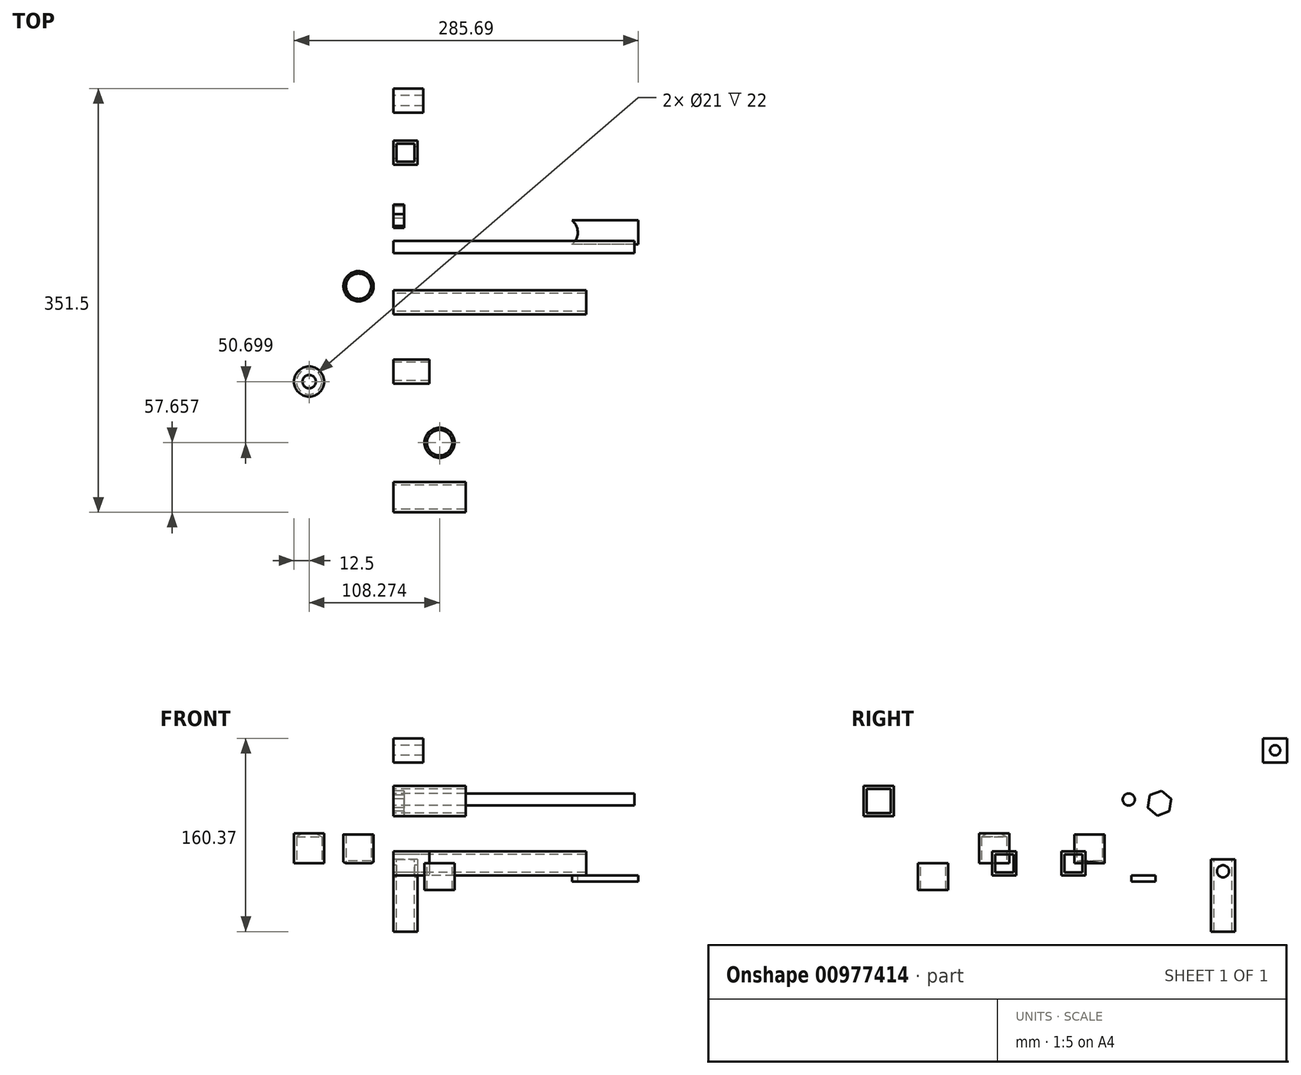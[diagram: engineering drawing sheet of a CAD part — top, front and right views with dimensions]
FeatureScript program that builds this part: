
annotation { "Feature Type Name" : "Feature", "Feature Type Description" : "" }
export const myFeature = defineFeature(function(context is Context, id is Id, definition is map)
    precondition{}
    {
        {
            var Q0;
            Q0=qCreatedBy(makeId("Front.planeOp"),FACE);
            var sketch = newSketch(context, id + "F0", { "sketchPlane" : qUnion([Q0])});
            skLineSegment(sketch, "E0.bottom", {"start": v(160, 10) * mm, "end": v(0, 10) * mm});
            skLineSegment(sketch, "E0.top", {"start": v(160, -10) * mm, "end": v(0, -10) * mm});
            skLineSegment(sketch, "E0.left", {"start": v(160, 10) * mm, "end": v(160, -10) * mm});
            skLineSegment(sketch, "E0.right", {"start": v(0, 10) * mm, "end": v(0, -10) * mm});
            skPoint(sketch, "E0.middle", {"position": v(80, 0) * mm});
            skSolve(sketch);
        }
        {
            var Q0;
            Q0 = qSketchRegion(id + "F0", true);
            extrude(context, id + "F1", {"entities" : qUnion([Q0]), "endBound" : BoundingType.SYMMETRIC, "depth" : 20 * mm, "offsetDistance" : 25 * mm});
        }
        {
            var Q0;
            Q0=qCreatedBy(makeId("Right.planeOp"),FACE);
            var sketch = newSketch(context, id + "F2", { "sketchPlane" : qUnion([Q0])});
            skLineSegment(sketch, "E1.bottom", {"start": v(-149.11, 64.26) * mm, "end": v(-174.11, 64.26) * mm});
            skLineSegment(sketch, "E1.top", {"start": v(-149.11, 39.26) * mm, "end": v(-174.11, 39.26) * mm});
            skLineSegment(sketch, "E1.left", {"start": v(-149.11, 64.26) * mm, "end": v(-149.11, 39.26) * mm});
            skLineSegment(sketch, "E1.right", {"start": v(-174.11, 64.26) * mm, "end": v(-174.11, 39.26) * mm});
            skPoint(sketch, "E1.middle", {"position": v(-161.61, 51.76) * mm});
            skLineSegment(sketch, "E2.bottom", {"start": v(-151.61, 61.76) * mm, "end": v(-171.61, 61.76) * mm});
            skLineSegment(sketch, "E2.top", {"start": v(-151.61, 41.76) * mm, "end": v(-171.61, 41.76) * mm});
            skLineSegment(sketch, "E2.left", {"start": v(-151.61, 61.76) * mm, "end": v(-151.61, 41.76) * mm});
            skLineSegment(sketch, "E2.right", {"start": v(-171.61, 61.76) * mm, "end": v(-171.61, 41.76) * mm});
            skSolve(sketch);
        }
        {
            var Q0;
            Q0 = qSketchRegion(id + "F2", true);
            extrude(context, id + "F3", {"entities" : qUnion([Q0]), "depth" : 60 * mm, "offsetDistance" : 25 * mm});
        }
        {
            var Q0;
            Q0=qCreatedBy(makeId("Right.planeOp"),FACE);
            var sketch = newSketch(context, id + "F4", { "sketchPlane" : qUnion([Q0])});
            skLineSegment(sketch, "E3.bottom", {"start": v(-7.5, 7.5) * mm, "end": v(7.5, 7.5) * mm});
            skLineSegment(sketch, "E3.top", {"start": v(-7.5, -7.5) * mm, "end": v(7.5, -7.5) * mm});
            skLineSegment(sketch, "E3.left", {"start": v(-7.5, 7.5) * mm, "end": v(-7.5, -7.5) * mm});
            skLineSegment(sketch, "E3.right", {"start": v(7.5, 7.5) * mm, "end": v(7.5, -7.5) * mm});
            skPoint(sketch, "E3.middle", {"position": v(0, 0) * mm});
            skSolve(sketch);
        }
        {
            var Q0;
            Q0 = qSketchRegion(id + "F4", true);
            extrude(context, id + "F5", {"entities" : qUnion([Q0]), "operationType" : NewBodyOperationType.REMOVE, "depth" : 160 * mm, "offsetDistance" : 25 * mm});
        }
        {
            var Q0;
            Q0=qCreatedBy(makeId("Right.planeOp"),FACE);
            var sketch = newSketch(context, id + "F6", { "sketchPlane" : qUnion([Q0])});
            skLineSegment(sketch, "E4.bottom", {"start": v(-67.3, 9.88) * mm, "end": v(-47.3, 9.88) * mm});
            skLineSegment(sketch, "E4.top", {"start": v(-67.3, -10.12) * mm, "end": v(-47.3, -10.12) * mm});
            skLineSegment(sketch, "E4.left", {"start": v(-67.3, 9.88) * mm, "end": v(-67.3, -10.12) * mm});
            skLineSegment(sketch, "E4.right", {"start": v(-47.3, 9.88) * mm, "end": v(-47.3, -10.12) * mm});
            skPoint(sketch, "E4.middle", {"position": v(-57.3, -0.12) * mm});
            skLineSegment(sketch, "E5.bottom", {"start": v(-64.8, 7.38) * mm, "end": v(-49.8, 7.38) * mm});
            skLineSegment(sketch, "E5.top", {"start": v(-64.8, -7.62) * mm, "end": v(-49.8, -7.62) * mm});
            skLineSegment(sketch, "E5.left", {"start": v(-64.8, 7.38) * mm, "end": v(-64.8, -7.62) * mm});
            skLineSegment(sketch, "E5.right", {"start": v(-49.8, 7.38) * mm, "end": v(-49.8, -7.62) * mm});
            skSolve(sketch);
        }
        {
            var Q0;
            Q0 = qSketchRegion(id + "F6", true);
            extrude(context, id + "F7", {"entities" : qUnion([Q0]), "depth" : 30 * mm, "offsetDistance" : 25 * mm});
        }
        {
            var Q0;
            Q0=qCreatedBy(makeId("Top.planeOp"),FACE);
            var sketch = newSketch(context, id + "F8", { "sketchPlane" : qUnion([Q0])});
            skCircle(sketch, "E6", {"center": v(38.4, -116.45) * mm, "radius": 12.5 * mm});
            skCircle(sketch, "E7", {"center": v(38.4, -116.45) * mm, "radius": 10.5 * mm});
            skSolve(sketch);
        }
        {
            var Q0;
            Q0 = qSketchRegion(id + "F8", true);
            extrude(context, id + "F9", {"entities" : qUnion([Q0]), "oppositeDirection" : true, "depth" : 22 * mm, "offsetDistance" : 25 * mm});
        }
        {
            var Q0;
            Q0=qCreatedBy(makeId("Top.planeOp"),FACE);
            var sketch = newSketch(context, id + "F10", { "sketchPlane" : qUnion([Q0])});
            skCircle(sketch, "E8", {"center": v(-28.9, 13.35) * mm, "radius": 12.5 * mm});
            skCircle(sketch, "E9", {"center": v(-28.9, 13.35) * mm, "radius": 10.5 * mm});
            skSolve(sketch);
        }
        {
            var Q0;
            Q0 = qSketchRegion(id + "F10", true);
            extrude(context, id + "F11", {"entities" : qUnion([Q0]), "operationType" : NewBodyOperationType.ADD, "depth" : 24 * mm, "offsetDistance" : 25 * mm});
        }
        {
            var Q0;
            Q0=qCreatedBy(makeId("Top.planeOp"),FACE);
            var sketch = newSketch(context, id + "F12", { "sketchPlane" : qUnion([Q0])});
            skCircle(sketch, "E10", {"center": v(-69.87, -65.75) * mm, "radius": 12.5 * mm});
            skSolve(sketch);
        }
        {
            var Q0;
            Q0=makeQuery(id+"F12.imprint","IMPRINT",FACE,{"disambiguationData":[TD([[makeQuery(id+"F12.imprint","IMPRINT",EDGE,{"derivedFrom":sQuery(id+"F12.wireOp",EDGE,"E10")}),1.0]])]});
            var Q1;
            Q1=sQuery(id+"F12.wireOp",EDGE,"E10");
            extrude(context, id + "F13", {"entities" : qUnion([Q0]), "surfaceEntities" : qUnion([Q1]), "depth" : 25 * mm, "offsetDistance" : 25 * mm});
        }
        {
            var Q0;
            Q0=sQuery(id+"F12.wireOp",VERTEX,"E10.center");
            var Q1;
            Q1=makeQuery(id+"F13.opExtrude","SWEPT_BODY",BODY,{"disambiguationData":[OSD([sQuery(id+"F12.wireOp",EDGE,"E10")])]});
            hole(context, id + "F14", {"style" : HoleStyle.SIMPLE, "endStyle" : HoleEndStyle.BLIND, "oppositeDirection" : true, "holeDiameter" : 21 * mm, "majorDiameter" : 5 * mm, "holeDepth" : 22 * mm, "isTappedThrough" : true, "tappedDepth" : 12 * mm, "tapClearance" : 3, "locations" : qUnion([Q0]), "scope" : qUnion([Q1])});
        }
        {
            var Q0;
            Q0=makeQuery(id+"F1.opExtrude","SWEPT_FACE",FACE,{"disambiguationData":[OSD([sQuery(id+"F0.wireOp",EDGE,"E0.top")])]});
            var sketch = newSketch(context, id + "F15", { "sketchPlane" : qUnion([Q0])});
            skLineSegment(sketch, "E11.bottom", {"start": v(203.32, -48.1) * mm, "end": v(148.32, -48.1) * mm});
            skLineSegment(sketch, "E11.top", {"start": v(203.32, -68.1) * mm, "end": v(148.32, -68.1) * mm});
            skLineSegment(sketch, "E11.left", {"start": v(203.32, -48.1) * mm, "end": v(203.32, -68.1) * mm});
            skLineSegment(sketch, "E11.right", {"start": v(148.32, -48.1) * mm, "end": v(148.32, -68.1) * mm});
            skPoint(sketch, "E11.middle", {"position": v(175.82, -58.1) * mm});
            skSolve(sketch);
        }
        {
            var Q0;
            Q0 = qSketchRegion(id + "FznQOVtNDYuo7BJ_6", true);
            var Q1;
            Q1=makeQuery(id+"F15.imprint","IMPRINT",FACE,{"disambiguationData":[TD([[makeQuery(id+"F15.imprint","IMPRINT",EDGE,{"derivedFrom":sQuery(id+"F15.wireOp",EDGE,"E11.bottom")}),1.0]])]});
            extrude(context, id + "F16", {"entities" : qUnion([Q0, Q1]), "depth" : 5 * mm, "offsetDistance" : 25 * mm});
        }
        {
            var Q0;
            Q0=qCreatedBy(makeId("Right.planeOp"),FACE);
            var sketch = newSketch(context, id + "F17", { "sketchPlane" : qUnion([Q0])});
            skLineSegment(sketch, "E12.bottom", {"start": v(134.15, 3.4) * mm, "end": v(114.15, 3.4) * mm});
            skLineSegment(sketch, "E12.top", {"start": v(134.15, -56.6) * mm, "end": v(114.15, -56.6) * mm});
            skLineSegment(sketch, "E12.left", {"start": v(134.15, 3.4) * mm, "end": v(134.15, -56.6) * mm});
            skLineSegment(sketch, "E12.right", {"start": v(114.15, 3.4) * mm, "end": v(114.15, -56.6) * mm});
            skPoint(sketch, "E12.middle", {"position": v(124.15, -26.6) * mm});
            skPoint(sketch, "E13", {"position": v(124.15, -6.6) * mm});
            skCircle(sketch, "E14", {"center": v(124.15, -6.6) * mm, "radius": 5 * mm});
            skSolve(sketch);
        }
        {
            var Q0;
            Q0 = qSketchRegion(id + "F17", true);
            extrude(context, id + "F18", {"entities" : qUnion([Q0]), "depth" : 20 * mm, "offsetDistance" : 25 * mm});
        }
        {
            var Q0;
            Q0=qCreatedBy(makeId("Right.planeOp"),FACE);
            var sketch = newSketch(context, id + "F19", { "sketchPlane" : qUnion([Q0])});
            skLineSegment(sketch, "E15.bottom", {"start": v(177.39, 103.76) * mm, "end": v(157.39, 103.76) * mm});
            skLineSegment(sketch, "E15.top", {"start": v(177.39, 83.76) * mm, "end": v(157.39, 83.76) * mm});
            skLineSegment(sketch, "E15.left", {"start": v(177.39, 103.76) * mm, "end": v(177.39, 83.76) * mm});
            skLineSegment(sketch, "E15.right", {"start": v(157.39, 103.76) * mm, "end": v(157.39, 83.76) * mm});
            skPoint(sketch, "E15.middle", {"position": v(167.39, 93.76) * mm});
            skSolve(sketch);
        }
        {
            var Q0;
            Q0=makeQuery(id+"F19.imprint","IMPRINT",FACE,{"disambiguationData":[TD([[makeQuery(id+"F19.imprint","IMPRINT",EDGE,{"derivedFrom":sQuery(id+"F19.wireOp",EDGE,"E15.bottom")}),1.0]])]});
            var Q1;
            Q1=makeQuery(id+"F19.imprint","IMPRINT",FACE,{"disambiguationData":[TD([[makeQuery(id+"F19.imprint","IMPRINT",EDGE,{"derivedFrom":sQuery(id+"F19.wireOp",EDGE,"7127c330-42ca-4884-bdbb-8791a35309d2")}),1.0]])]});
            extrude(context, id + "F20", {"entities" : qUnion([Q0, Q1]), "depth" : 25 * mm, "offsetDistance" : 25 * mm});
        }
        {
            var Q0;
            Q0=sQuery(id+"F19.wireOp",VERTEX,"E15.middle");
            var Q1;
            Q1=makeQuery(id+"F20.opExtrude","SWEPT_BODY",BODY,{"disambiguationData":[OSD([sQuery(id+"F19.wireOp",EDGE,"E15.bottom"),sQuery(id+"F19.wireOp",EDGE,"E15.top"),sQuery(id+"F19.wireOp",EDGE,"E15.left"),sQuery(id+"F19.wireOp",EDGE,"E15.right")])]});
            hole(context, id + "F21", {"style" : HoleStyle.SIMPLE, "endStyle" : HoleEndStyle.THROUGH, "oppositeDirection" : true, "standardTappedOrClearance" : lookupTablePath({ "fit" : "Normal", "standard" : "ISO", "engagement" : "75%", "pitch" : "1.5 mm", "size" : "M10", "type" : "Tapped" }), "standardBlindInLast" : lookupTablePath({ "fit" : "Normal", "standard" : "ISO", "engagement" : "75%", "pitch" : "1.5 mm", "size" : "M10", "type" : "Clearance & tapped" }), "holeDiameter" : 8.5 * mm, "majorDiameter" : 10 * mm, "showTappedDepth" : true, "isTappedThrough" : true, "tappedDepth" : 12 * mm, "tapClearance" : 3, "locations" : qUnion([Q0]), "scope" : qUnion([Q1])});
        }
        {
            var Q0;
            Q0=qCreatedBy(makeId("Right.planeOp"),FACE);
            var sketch = newSketch(context, id + "F22", { "sketchPlane" : qUnion([Q0])});
            skCircle(sketch, "E16", {"center": v(45.93, 52.95) * mm, "radius": 5 * mm});
            skSolve(sketch);
        }
        {
            var Q0;
            Q0=makeQuery(id+"F22.imprint","IMPRINT",FACE,{"disambiguationData":[TD([[makeQuery(id+"F22.imprint","IMPRINT",EDGE,{"derivedFrom":sQuery(id+"F22.wireOp",EDGE,"E16")}),1.0]])]});
            extrude(context, id + "F23", {"entities" : qUnion([Q0]), "depth" : 200 * mm, "offsetDistance" : 25 * mm});
        }
        {
            var Q0;
            Q0=qCreatedBy(makeId("Right.planeOp"),FACE);
            var sketch = newSketch(context, id + "F24", { "sketchPlane" : qUnion([Q0])});
            skCircle(sketch, "E17.cCircle", {"center": v(71.45, 49.81) * mm, "radius": 10.4 * mm, "construction": true});
            skLineSegment(sketch, "E17.0", {"start": v(81.21, 53.37) * mm, "end": v(79.42, 43.14) * mm});
            skLineSegment(sketch, "E17.1", {"start": v(79.42, 43.14) * mm, "end": v(69.65, 39.58) * mm});
            skLineSegment(sketch, "E17.2", {"start": v(69.65, 39.58) * mm, "end": v(61.69, 46.25) * mm});
            skLineSegment(sketch, "E17.3", {"start": v(61.69, 46.25) * mm, "end": v(63.48, 56.49) * mm});
            skLineSegment(sketch, "E17.4", {"start": v(63.48, 56.49) * mm, "end": v(73.25, 60.05) * mm});
            skLineSegment(sketch, "E17.5", {"start": v(73.25, 60.05) * mm, "end": v(81.21, 53.37) * mm});
            skSolve(sketch);
        }
        {
            var Q0;
            Q0 = qSketchRegion(id + "F24", true);
            extrude(context, id + "F25", {"entities" : qUnion([Q0]), "depth" : 9 * mm, "offsetDistance" : 25 * mm});
        }
        {
            var Q0;
            Q0=qCreatedBy(makeId("Front.planeOp"),FACE);
            var sketch = newSketch(context, id + "F26", { "sketchPlane" : qUnion([Q0])});
            skLineSegment(sketch, "E18", {"start": v(-16.4, 0) * mm, "end": v(-18.4, 0) * mm});
            skLineSegment(sketch, "E19", {"start": v(-18.4, 0) * mm, "end": v(-16.4, 1.15) * mm});
            skLineSegment(sketch, "E20", {"start": v(-16.4, 1.15) * mm, "end": v(-16.4, 0) * mm});
            skLineSegment(sketch, "E21", {"start": v(-16.4, 24) * mm, "end": v(-16.4, 0) * mm});
            skSolve(sketch);
        }
        {
            var Q0;
            Q0 = qSketchRegion(id + "F26", true);
            extrude(context, id + "F27", {"entities" : qUnion([Q0]), "operationType" : NewBodyOperationType.REMOVE, "oppositeDirection" : true, "depth" : 25 * mm, "offsetDistance" : 25 * mm});
        }
        {
            var Q0;
            Q0=qCreatedBy(makeId("Front.planeOp"),FACE);
            var sketch = newSketch(context, id + "F28", { "sketchPlane" : qUnion([Q0])});
            skLineSegment(sketch, "E22", {"start": v(-41.4, 0) * mm, "end": v(-39.4, 0) * mm});
            skLineSegment(sketch, "E23", {"start": v(-39.4, 0) * mm, "end": v(-41.4, 1.15) * mm});
            skLineSegment(sketch, "E24", {"start": v(-41.4, 1.15) * mm, "end": v(-41.4, 0) * mm});
            skLineSegment(sketch, "E25", {"start": v(-41.4, 0) * mm, "end": v(-41.4, 24) * mm});
            skSolve(sketch);
        }
        {
            var Q0;
            Q0 = qSketchRegion(id + "F28", true);
            extrude(context, id + "F29", {"entities" : qUnion([Q0]), "operationType" : NewBodyOperationType.REMOVE, "oppositeDirection" : true, "depth" : 25 * mm, "offsetDistance" : 25 * mm});
        }
        {
            var Q0;
            Q0=qCreatedBy(makeId("Top.planeOp"),FACE);
            var sketch = newSketch(context, id + "F30", { "sketchPlane" : qUnion([Q0])});
            skCircle(sketch, "E26", {"center": v(-28.8, 13.38) * mm, "radius": 10.5 * mm});
            skSolve(sketch);
        }
        {
            var Q0;
            Q0 = qSketchRegion(id + "F30", true);
            extrude(context, id + "F31", {"entities" : qUnion([Q0]), "depth" : 2 * mm, "offsetDistance" : 25 * mm});
        }
        {
            var Q0;
            Q0=makeQuery(id+"F18.opExtrude","SWEPT_FACE",FACE,{"disambiguationData":[OSD([sQuery(id+"F17.wireOp",EDGE,"E12.bottom")])]});
            var sketch = newSketch(context, id + "F32", { "sketchPlane" : qUnion([Q0])});
            skLineSegment(sketch, "E27.bottom", {"start": v(2.52, 131.57) * mm, "end": v(17.52, 131.57) * mm});
            skLineSegment(sketch, "E27.top", {"start": v(2.52, 116.57) * mm, "end": v(17.52, 116.57) * mm});
            skLineSegment(sketch, "E27.left", {"start": v(2.52, 131.57) * mm, "end": v(2.52, 116.57) * mm});
            skLineSegment(sketch, "E27.right", {"start": v(17.52, 131.57) * mm, "end": v(17.52, 116.57) * mm});
            skPoint(sketch, "E27.middle", {"position": v(10.02, 124.07) * mm});
            skSolve(sketch);
        }
        {
            var Q0;
            Q0=makeQuery(id+"F32.imprint","IMPRINT",FACE,{"disambiguationData":[TD([[makeQuery(id+"F32.imprint","IMPRINT",EDGE,{"derivedFrom":sQuery(id+"F32.wireOp",EDGE,"E27.bottom")}),-1.0]])]});
            extrude(context, id + "F33", {"entities" : qUnion([Q0]), "operationType" : NewBodyOperationType.REMOVE, "oppositeDirection" : true, "depth" : 60 * mm, "offsetDistance" : 25 * mm});
        }
        {
            var Q0;
            Q0=makeQuery(id+"F15.imprint","IMPRINT",FACE,{"disambiguationData":[TD([[makeQuery(id+"F15.imprint","IMPRINT",EDGE,{"derivedFrom":sQuery(id+"F15.wireOp",EDGE,"E11.bottom")}),1.0]])]});
            var sketch = newSketch(context, id + "F34", { "sketchPlane" : qUnion([Q0])});
            skCircle(sketch, "E28", {"center": v(140.33, -58.08) * mm, "radius": 12.75 * mm});
            skSolve(sketch);
        }
        {
            var Q0;
            Q0 = qSketchRegion(id + "F34", true);
            extrude(context, id + "F35", {"entities" : qUnion([Q0]), "operationType" : NewBodyOperationType.REMOVE, "depth" : 5 * mm, "offsetDistance" : 25 * mm});
        }
    });
